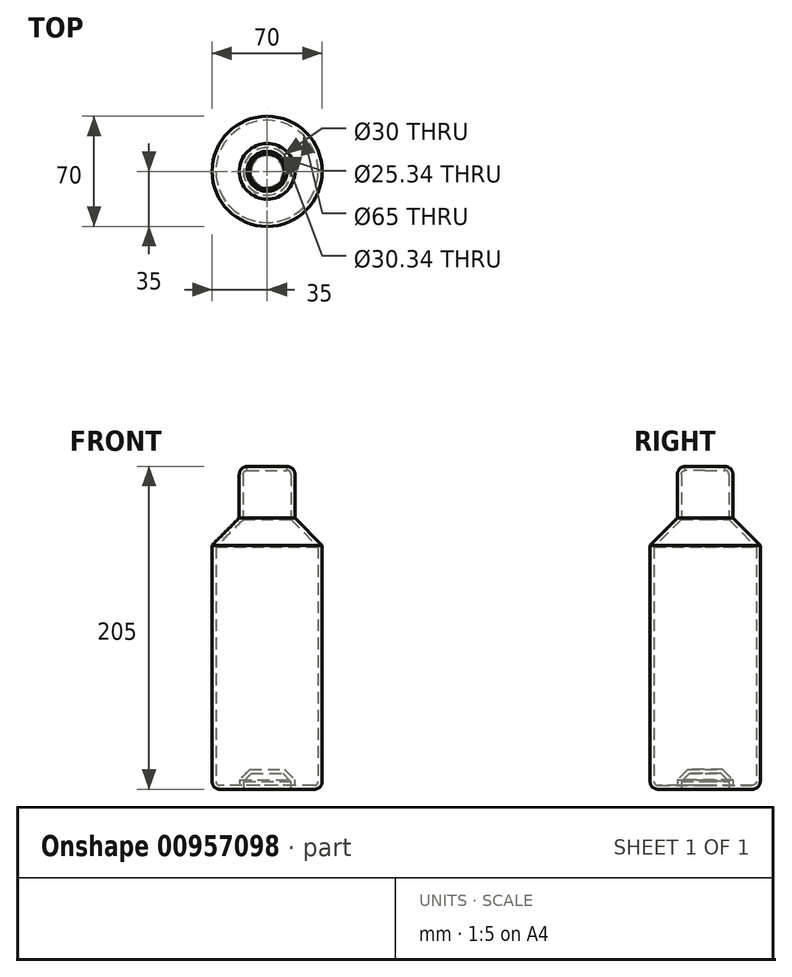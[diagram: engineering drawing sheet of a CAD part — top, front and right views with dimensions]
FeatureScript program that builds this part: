
annotation { "Feature Type Name" : "Feature", "Feature Type Description" : "" }
export const myFeature = defineFeature(function(context is Context, id is Id, definition is map)
    precondition{}
    {
        {
            var Q0;
            Q0=qCreatedBy(makeId("Top.planeOp"),FACE);
            var sketch = newSketch(context, id + "F0", { "sketchPlane" : qUnion([Q0])});
            skCircle(sketch, "E0", {"center": v(0, 0) * mm, "radius": 35 * mm});
            skSolve(sketch);
        }
        {
            var Q0;
            Q0=makeQuery(id+"F0.imprint","IMPRINT",FACE,{"disambiguationData":[TD([[makeQuery(id+"F0.imprint","IMPRINT",EDGE,{"derivedFrom":sQuery(id+"F0.wireOp",EDGE,"E0")}),1.0]])]});
            extrude(context, id + "F1", {"entities" : qUnion([Q0]), "depth" : 180 * mm, "offsetDistance" : 25 * mm});
        }
        {
            var Q0;
            Q0=makeQuery(id+"F1.opExtrude","CAP_FACE",FACE,{"disambiguationData":[OSD([sQuery(id+"F0.wireOp",EDGE,"E0")])],"isStart":true});
            var sketch = newSketch(context, id + "F2", { "sketchPlane" : qUnion([Q0])});
            skCircle(sketch, "E1", {"center": v(0, 0) * mm, "radius": 15 * mm});
            skSolve(sketch);
        }
        {
            var Q0;
            Q0=makeQuery(id+"F2.imprint","IMPRINT",FACE,{"disambiguationData":[TD([[makeQuery(id+"F2.imprint","IMPRINT",EDGE,{"derivedFrom":sQuery(id+"F2.wireOp",EDGE,"E1")}),1.0]])]});
            extrude(context, id + "F3", {"entities" : qUnion([Q0]), "operationType" : NewBodyOperationType.REMOVE, "oppositeDirection" : true, "depth" : 10 * mm, "offsetDistance" : 25 * mm});
        }
        {
            var Q0;
            Q0=makeQuery(id+"F3.boolean.opBoolean","COPY",FACE,{"derivedFrom":makeQuery(id+"F3.opExtrude","CAP_FACE",FACE,{"disambiguationData":[OSD([sQuery(id+"F2.wireOp",EDGE,"E1")])],"isStart":false})});
            var Q1;
            Q1=makeQuery(id+"F3.boolean.opBoolean","COPY",EDGE,{"derivedFrom":makeQuery(id+"F3.opExtrude","CAP_EDGE",EDGE,{"disambiguationData":[OSD([sQuery(id+"F2.wireOp",EDGE,"E1")])],"isStart":true})});
            chamfer(context, id + "F4", {"entities" : qUnion([Q0, Q1]), "width" : 5 * mm, "tangentPropagation" : true});
        }
        {
            var Q0;
            Q0=makeQuery(id+"F1.opExtrude","CAP_FACE",FACE,{"disambiguationData":[OSD([sQuery(id+"F0.wireOp",EDGE,"E0")])],"isStart":false});
            var sketch = newSketch(context, id + "F5", { "sketchPlane" : qUnion([Q0])});
            skCircle(sketch, "E2", {"center": v(0, 0) * mm, "radius": 17.67 * mm});
            skSolve(sketch);
        }
        {
            var Q0;
            Q0=makeQuery(id+"F5.imprint","IMPRINT",FACE,{"disambiguationData":[TD([[makeQuery(id+"F5.imprint","IMPRINT",EDGE,{"derivedFrom":sQuery(id+"F5.wireOp",EDGE,"E2")}),1.0]])]});
            extrude(context, id + "F6", {"entities" : qUnion([Q0]), "operationType" : NewBodyOperationType.ADD, "depth" : 25 * mm, "offsetDistance" : 25 * mm});
        }
        {
            var Q0;
            Q0=makeQuery(id+"F6.opExtrude","CAP_FACE",FACE,{"disambiguationData":[OSD([sQuery(id+"F5.wireOp",EDGE,"E2")])],"isStart":false});
            fillet(context, id + "F7", {"entities" : qUnion([Q0]), "radius" : 5 * mm, "tangentPropagation" : true, "allowEdgeOverflow" : false});
        }
        {
            var Q0;
            Q0=makeQuery(id+"F1.opExtrude","CAP_EDGE",EDGE,{"disambiguationData":[OSD([sQuery(id+"F0.wireOp",EDGE,"E0")])],"isStart":true});
            fillet(context, id + "F8", {"entities" : qUnion([Q0]), "radius" : 5 * mm, "tangentPropagation" : true, "allowEdgeOverflow" : false});
        }
        {
            var Q0;
            Q0=makeQuery(id+"F1.opExtrude","CAP_EDGE",EDGE,{"disambiguationData":[OSD([sQuery(id+"F0.wireOp",EDGE,"E0")])],"isStart":false});
            chamfer(context, id + "F9", {"entities" : qUnion([Q0]), "width" : 25 * mm, "tangentPropagation" : true});
        }
        {
            var Q0;
            Q0=makeQuery(id+"F6.opExtrude","CAP_FACE",FACE,{"disambiguationData":[OSD([sQuery(id+"F5.wireOp",EDGE,"E2")])],"isStart":false});
            shell(context, id + "F10", {"entities" : qUnion([Q0]), "thickness" : 2.5 * mm});
        }
    });
